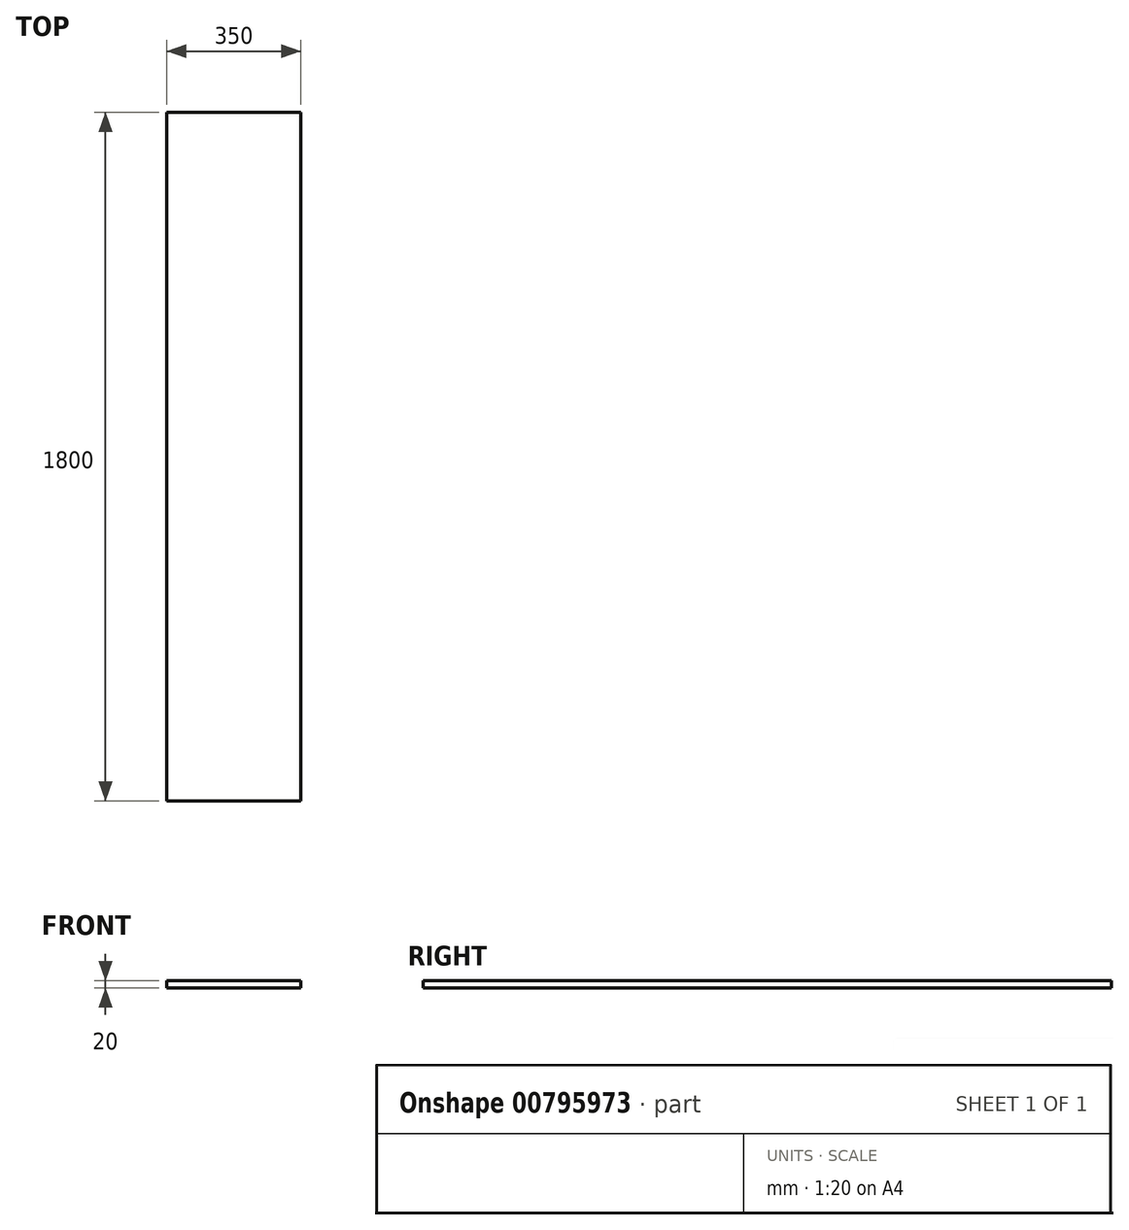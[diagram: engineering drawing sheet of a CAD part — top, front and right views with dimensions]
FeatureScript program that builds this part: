
annotation { "Feature Type Name" : "Feature", "Feature Type Description" : "" }
export const myFeature = defineFeature(function(context is Context, id is Id, definition is map)
    precondition{}
    {
        {
            var Q0;
            Q0=qCreatedBy(makeId("Top.planeOp"),FACE);
            var sketch = newSketch(context, id + "F0", { "sketchPlane" : qUnion([Q0])});
            skLineSegment(sketch, "E0.bottom", {"start": v(0, 0) * mm, "end": v(350, 0) * mm});
            skLineSegment(sketch, "E0.top", {"start": v(0, 1800) * mm, "end": v(350, 1800) * mm});
            skLineSegment(sketch, "E0.left", {"start": v(0, 0) * mm, "end": v(0, 1800) * mm});
            skLineSegment(sketch, "E0.right", {"start": v(350, 0) * mm, "end": v(350, 1800) * mm});
            skSolve(sketch);
        }
        {
            var Q0;
            Q0=makeQuery(id+"F0.imprint","IMPRINT",FACE,{"disambiguationData":[TD([[makeQuery(id+"F0.imprint","IMPRINT",EDGE,{"derivedFrom":sQuery(id+"F0.wireOp",EDGE,"E0.bottom")}),1.0]])]});
            extrude(context, id + "F1", {"entities" : qUnion([Q0]), "depth" : 20 * mm, "offsetDistance" : 25 * mm});
        }
    });
